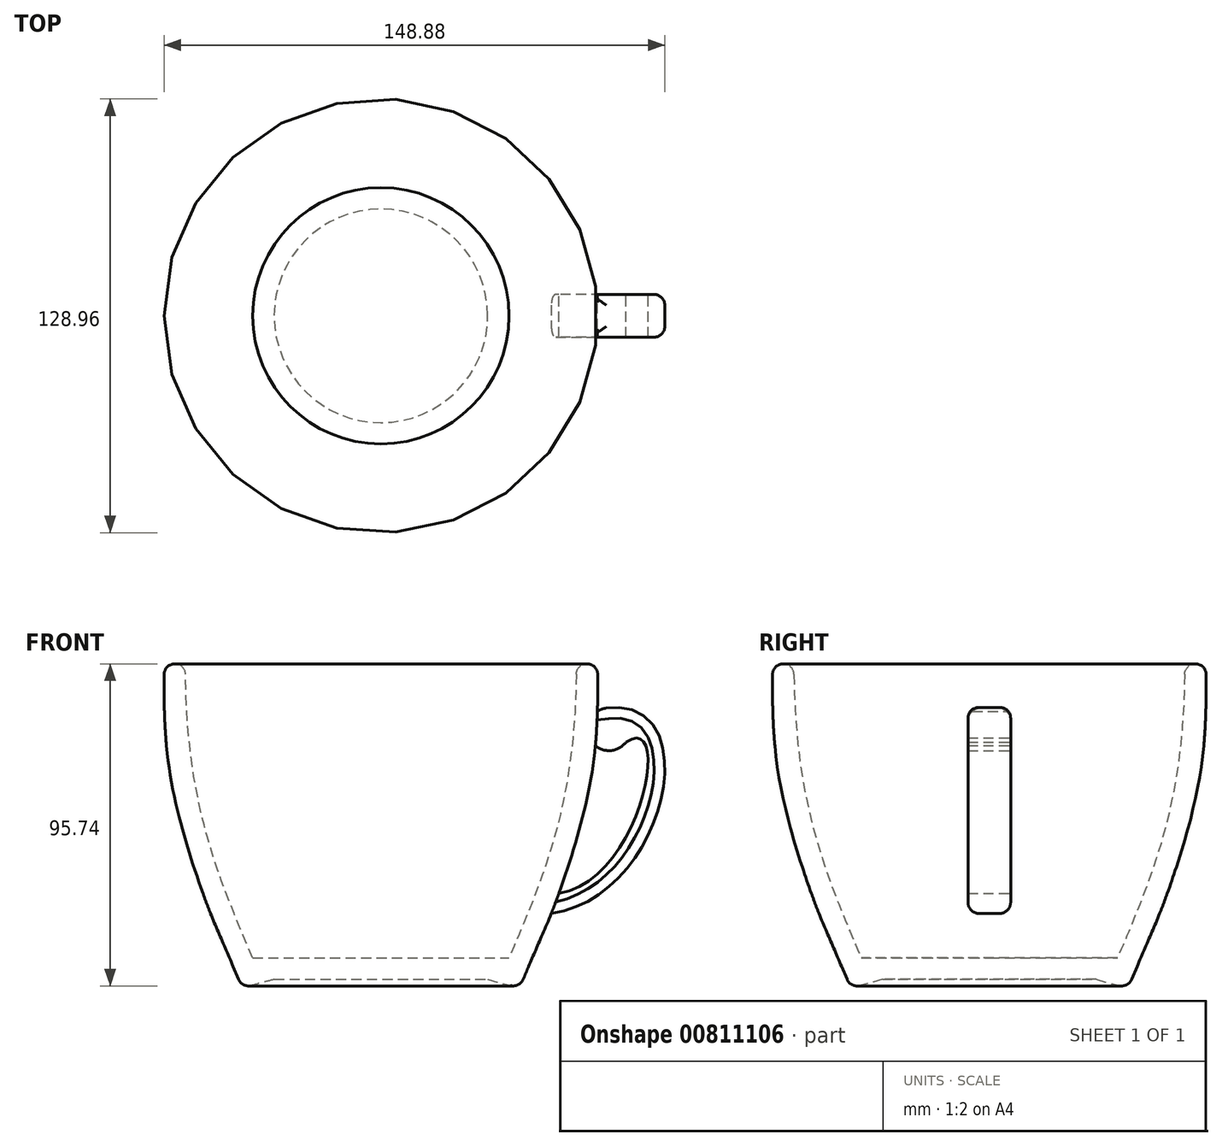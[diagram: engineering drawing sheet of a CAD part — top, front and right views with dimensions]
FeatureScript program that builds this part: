
annotation { "Feature Type Name" : "Feature", "Feature Type Description" : "" }
export const myFeature = defineFeature(function(context is Context, id is Id, definition is map)
    precondition{}
    {
        {
            var Q0;
            Q0=qCreatedBy(makeId("Front.planeOp"),FACE);
            var sketch = newSketch(context, id + "F0", { "sketchPlane" : qUnion([Q0])});
            skLineSegment(sketch, "E0", {"start": v(0, 0) * mm, "end": v(0, 6.35) * mm});
            skLineSegment(sketch, "E1", {"start": v(0, 6.35) * mm, "end": v(38.1, 6.35) * mm});
            skFitSpline(sketch, "E2", {"points": [v(38.1, 6.35) * mm, v(58.1, 93.81) * mm], "startDerivative": vector(34.3, 80.2) * mm, "endDerivative": vector(0, 118.8) * mm});
            skFitSpline(sketch, "E3.0", {"points": [v(43.94, 3.85) * mm, v(46.8, 10.55) * mm, v(50.88, 20.17) * mm, v(55.56, 33.29) * mm, v(59.64, 46.95) * mm, v(63.35, 65.66) * mm, v(64.45, 83.68) * mm, v(64.45, 93.81) * mm]});
            skLineSegment(sketch, "E4", {"start": v(58.1, 93.81) * mm, "end": v(64.45, 93.81) * mm});
            skPoint(sketch, "E5.endDerivative.orphan", {"position": v(44.18, 0) * mm});
            skLineSegment(sketch, "E6", {"start": v(43.94, 3.85) * mm, "end": v(41.2, -2.54) * mm});
            skLineSegment(sketch, "E7", {"start": v(0, 0) * mm, "end": v(31.75, 0) * mm});
            skLineSegment(sketch, "E8", {"start": v(31.75, 0) * mm, "end": v(41.2, -2.54) * mm});
            skArc(sketch, "E9", {"start": v(63.28, 69.9) * mm, "mid": v(68.24, 68.02) * mm, "end": v(72.9, 70.57) * mm});
            skFitSpline(sketch, "E10", {"points": [v(66.95, 80.65) * mm, v(50.48, 19.6) * mm], "startDerivative": vector(92.1, 12.42) * mm, "endDerivative": vector(-103.95, -13.88) * mm});
            skFitSpline(sketch, "E11", {"points": [v(72.9, 70.57) * mm, v(52.75, 25.53) * mm], "startDerivative": vector(41.78, 28.45) * mm, "endDerivative": vector(-74.55, -11.64) * mm});
            skArc(sketch, "E12.trimOffspring", {"start": v(66.95, 80.65) * mm, "mid": v(65.43, 80.25) * mm, "end": v(64.05, 79.48) * mm});
            skSolve(sketch);
        }
        {
            var Q0;
            Q0=makeQuery(id+"F0.imprint","IMPRINT",FACE,{"disambiguationData":[TD([[makeQuery(id+"F0.imprint","IMPRINT",EDGE,{"derivedFrom":sQuery(id+"F0.wireOp",EDGE,"E0")}),-1.0]])]});
            var Q1;
            Q1=sQuery(id+"F0.wireOp",EDGE,"E0");
            revolve(context, id + "F1", {"surfaceOperationType" : NewSurfaceOperationType.NEW, "entities" : qUnion([Q0]), "axis" : qUnion([Q1]), "revolveType" : RevolveType.FULL});
        }
        {
            var Q0;
            {var subQ0=sQuery(id+"F0.wireOp",EDGE,"E11");Q0=makeQuery(id+"F0.imprint","IMPRINT",FACE,{"disambiguationData":[TD([[makeQuery(id+"F0.imprint","IMPRINT",EDGE,{"derivedFrom":subQ0}),1.0]])]});}
            extrude(context, id + "F2", {"entities" : qUnion([Q0]), "operationType" : NewBodyOperationType.ADD, "endBound" : BoundingType.SYMMETRIC, "depth" : 12.7 * mm, "offsetDistance" : 25.4 * mm});
        }
        {
            var Q0;
            Q0=makeQuery(id+"F1.opRevolve","SWEPT_EDGE",EDGE,{"disambiguationData":[OSD([sQuery(id+"F0.wireOp",EDGE,"E3.0"),sQuery(id+"F0.wireOp",EDGE,"E4")])]});
            var Q1;
            Q1=makeQuery(id+"F1.opRevolve","SWEPT_EDGE",EDGE,{"disambiguationData":[OSD([sQuery(id+"F0.wireOp",EDGE,"E2"),sQuery(id+"F0.wireOp",EDGE,"E4")])]});
            var Q2;
            Q2=makeQuery(id+"F1.opRevolve","SWEPT_EDGE",EDGE,{"disambiguationData":[OSD([sQuery(id+"F0.wireOp",EDGE,"E6"),sQuery(id+"F0.wireOp",EDGE,"E8")])]});
            var Q3;
            Q3=makeQuery(id+"F2.opExtrude","CAP_EDGE",EDGE,{"disambiguationData":[OSD([sQuery(id+"F0.wireOp",EDGE,"E10")])],"isStart":false});
            var Q4;
            Q4=makeQuery(id+"F2.opExtrude","CAP_EDGE",EDGE,{"disambiguationData":[OSD([sQuery(id+"F0.wireOp",EDGE,"E10")])],"isStart":true});
            fillet(context, id + "F3", {"entities" : qUnion([Q0, Q1, Q2, Q3, Q4]), "radius" : 3.17 * mm, "tangentPropagation" : true, "allowEdgeOverflow" : false});
        }
    });
